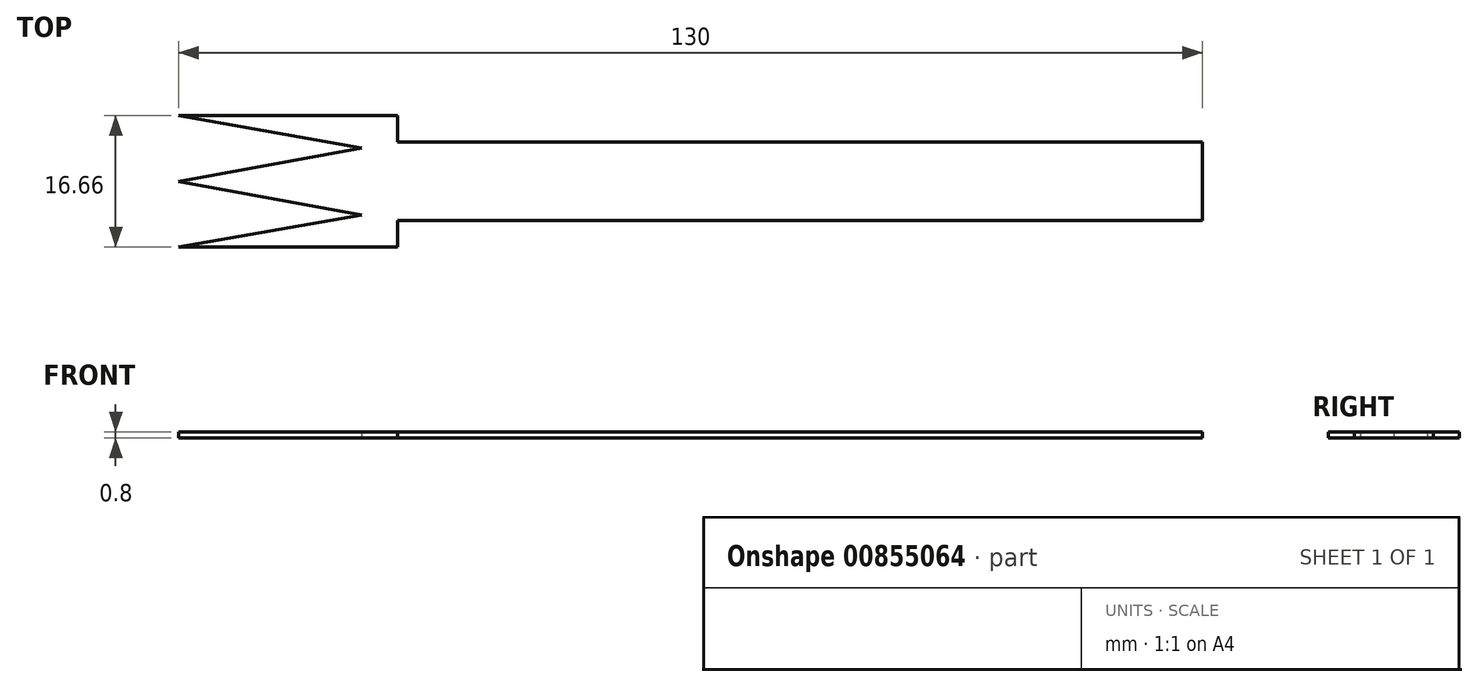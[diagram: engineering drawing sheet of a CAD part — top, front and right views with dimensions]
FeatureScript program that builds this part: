
annotation { "Feature Type Name" : "Feature", "Feature Type Description" : "" }
export const myFeature = defineFeature(function(context is Context, id is Id, definition is map)
    precondition{}
    {
        {
            var Q0;
            Q0=qCreatedBy(makeId("Top.planeOp"),FACE);
            var sketch = newSketch(context, id + "F0", { "sketchPlane" : qUnion([Q0])});
            skLineSegment(sketch, "E0.bottom", {"start": v(27.8, 5) * mm, "end": v(130, 5) * mm});
            skLineSegment(sketch, "E0.top", {"start": v(0, 0) * mm, "end": v(130, 0) * mm});
            skLineSegment(sketch, "E0.left", {"start": v(0, 5) * mm, "end": v(0, 0) * mm});
            skLineSegment(sketch, "E0.right", {"start": v(130, 5) * mm, "end": v(130, 0) * mm});
            skLineSegment(sketch, "E1.bottom", {"start": v(0, 8.33) * mm, "end": v(27.8, 8.33) * mm});
            skLineSegment(sketch, "E1.top", {"start": v(0, 0) * mm, "end": v(27.8, 0) * mm});
            skLineSegment(sketch, "E1.right", {"start": v(27.8, 8.33) * mm, "end": v(27.8, 5) * mm});
            skLineSegment(sketch, "E2", {"start": v(0, 8.33) * mm, "end": v(23.18, 4.25) * mm});
            skLineSegment(sketch, "E3", {"start": v(23.18, 4.25) * mm, "end": v(0, 0) * mm});
            skLineSegment(sketch, "E4.MirrorCS", {"start": v(27.8, -8.33) * mm, "end": v(27.8, -5) * mm});
            skLineSegment(sketch, "E5.MirrorCS", {"start": v(0, -5) * mm, "end": v(0, 0) * mm});
            skLineSegment(sketch, "E6.MirrorCS", {"start": v(0, -8.33) * mm, "end": v(27.8, -8.33) * mm});
            skLineSegment(sketch, "E7.MirrorCS", {"start": v(23.18, -4.25) * mm, "end": v(0, 0) * mm});
            skLineSegment(sketch, "E8.MirrorCS", {"start": v(27.8, -5) * mm, "end": v(130, -5) * mm});
            skLineSegment(sketch, "E9.MirrorCS", {"start": v(130, -5) * mm, "end": v(130, 0) * mm});
            skLineSegment(sketch, "E10.MirrorCS", {"start": v(0, -8.33) * mm, "end": v(23.18, -4.25) * mm});
            skSolve(sketch);
        }
        {
            var Q0;
            Q0 = qSketchRegion(id + "F0", true);
            extrude(context, id + "F1", {"entities" : qUnion([Q0]), "depth" : 0.8 * mm, "offsetDistance" : 25 * mm});
        }
    });
